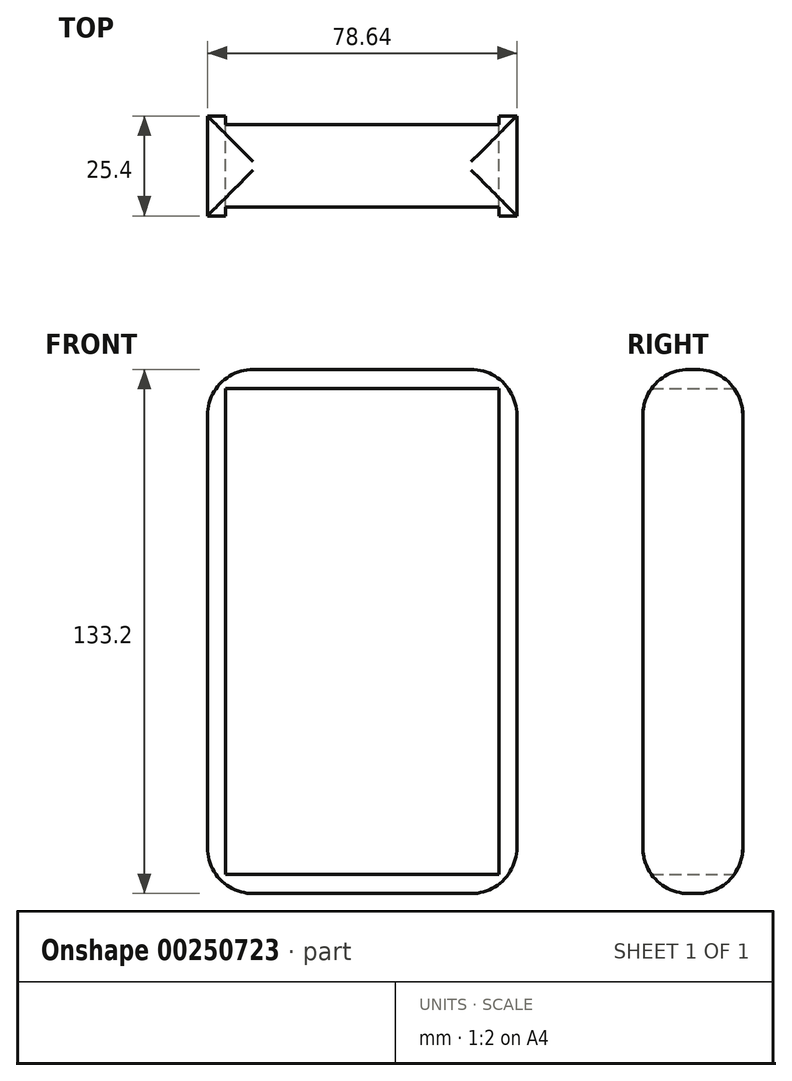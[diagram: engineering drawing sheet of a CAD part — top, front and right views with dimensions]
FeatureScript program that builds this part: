
annotation { "Feature Type Name" : "Feature", "Feature Type Description" : "" }
export const myFeature = defineFeature(function(context is Context, id is Id, definition is map)
    precondition{}
    {
        {
            var Q0;
            Q0=qCreatedBy(makeId("Front.planeOp"),FACE);
            var sketch = newSketch(context, id + "F0", { "sketchPlane" : qUnion([Q0])});
            skLineSegment(sketch, "E0.bottom", {"start": v(39.32, 66.6) * mm, "end": v(-39.32, 66.6) * mm});
            skLineSegment(sketch, "E0.top", {"start": v(39.32, -66.6) * mm, "end": v(-39.32, -66.6) * mm});
            skLineSegment(sketch, "E0.left", {"start": v(39.32, 66.6) * mm, "end": v(39.32, -66.6) * mm});
            skLineSegment(sketch, "E0.right", {"start": v(-39.32, 66.6) * mm, "end": v(-39.32, -66.6) * mm});
            skPoint(sketch, "E0.middle", {"position": v(0, 0) * mm});
            skLineSegment(sketch, "E1.bottom", {"start": v(34.75, 61.72) * mm, "end": v(-34.75, 61.72) * mm});
            skLineSegment(sketch, "E1.top", {"start": v(34.75, -61.72) * mm, "end": v(-34.75, -61.72) * mm});
            skLineSegment(sketch, "E1.left", {"start": v(34.75, 61.72) * mm, "end": v(34.75, -61.72) * mm});
            skLineSegment(sketch, "E1.right", {"start": v(-34.75, 61.72) * mm, "end": v(-34.75, -61.72) * mm});
            skSolve(sketch);
        }
        {
            var Q0;
            Q0=makeQuery(id+"F0.imprint","IMPRINT",FACE,{"disambiguationData":[TD([[makeQuery(id+"F0.imprint","IMPRINT",EDGE,{"derivedFrom":sQuery(id+"F0.wireOp",EDGE,"E0.bottom")}),1.0]])]});
            extrude(context, id + "F1", {"entities" : qUnion([Q0]), "endBound" : BoundingType.SYMMETRIC, "depth" : 25.4 * mm});
        }
        {
            var Q0;
            Q0=makeQuery(id+"F1.opExtrude","SWEPT_FACE",FACE,{"disambiguationData":[OSD([sQuery(id+"F0.wireOp",EDGE,"E0.bottom")])]});
            var Q1;
            Q1=makeQuery(id+"F1.opExtrude","SWEPT_FACE",FACE,{"disambiguationData":[OSD([sQuery(id+"F0.wireOp",EDGE,"E0.top")])]});
            fillet(context, id + "F2", {"entities" : qUnion([Q0, Q1]), "radius" : 11.65 * mm, "tangentPropagation" : true, "allowEdgeOverflow" : false});
        }
    });
